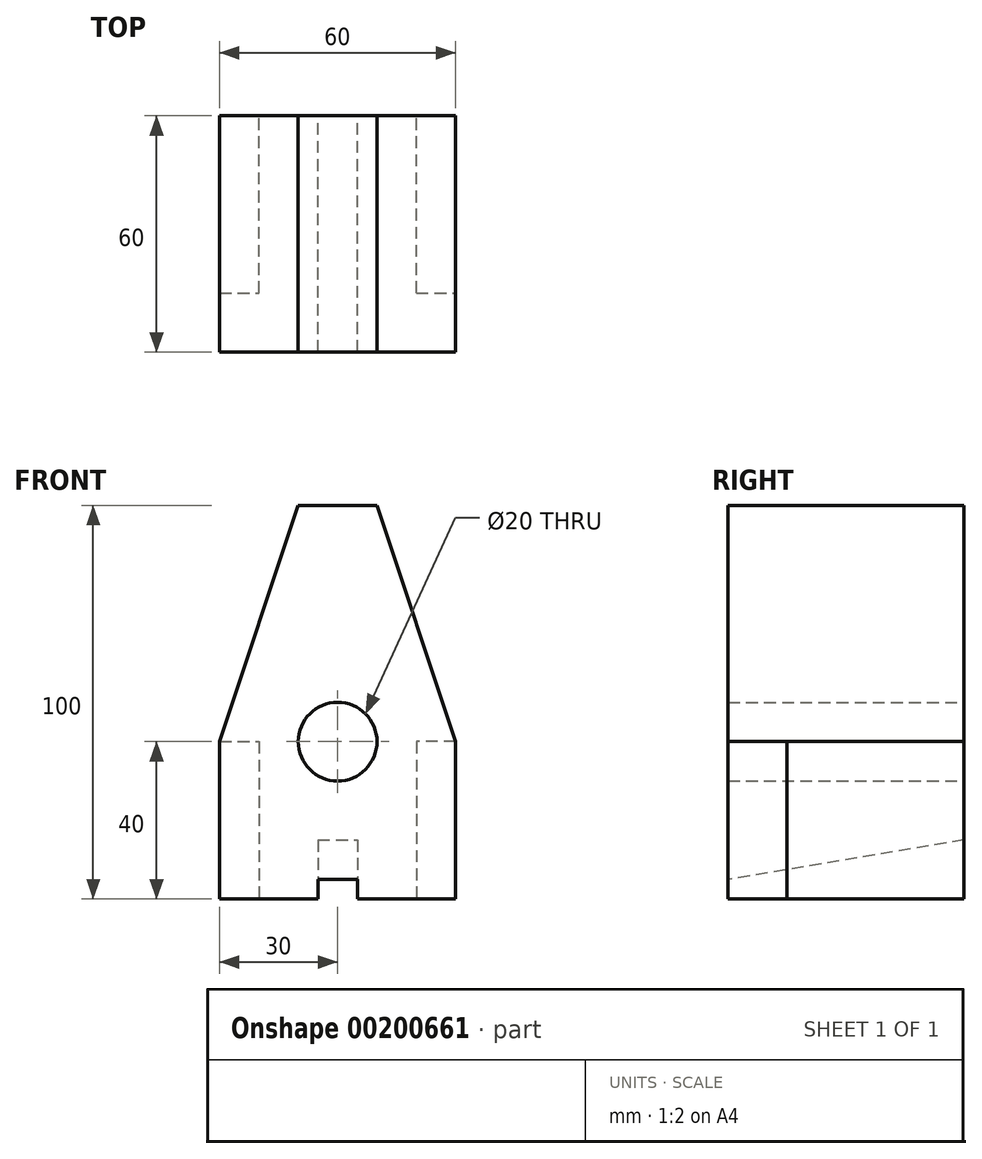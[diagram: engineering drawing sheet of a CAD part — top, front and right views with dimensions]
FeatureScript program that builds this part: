
annotation { "Feature Type Name" : "Feature", "Feature Type Description" : "" }
export const myFeature = defineFeature(function(context is Context, id is Id, definition is map)
    precondition{}
    {
        {
            var Q0;
            Q0=qCreatedBy(makeId("Front.planeOp"),FACE);
            var sketch = newSketch(context, id + "F0", { "sketchPlane" : qUnion([Q0])});
            skLineSegment(sketch, "E0", {"start": v(-30, 0) * mm, "end": v(30, 0) * mm});
            skLineSegment(sketch, "E1", {"start": v(-30, 0) * mm, "end": v(-30, 40) * mm});
            skLineSegment(sketch, "E2", {"start": v(-30, 40) * mm, "end": v(-10, 100) * mm});
            skLineSegment(sketch, "E3", {"start": v(-10, 100) * mm, "end": v(10, 100) * mm});
            skLineSegment(sketch, "E4", {"start": v(30, 0) * mm, "end": v(30, 40) * mm});
            skLineSegment(sketch, "E5", {"start": v(30, 40) * mm, "end": v(10, 100) * mm});
            skCircle(sketch, "E6", {"center": v(0, 40) * mm, "radius": 10 * mm});
            skSolve(sketch);
        }
        {
            var Q0;
            Q0=makeQuery(id+"F0.imprint","IMPRINT",FACE,{"disambiguationData":[TD([[makeQuery(id+"F0.imprint","IMPRINT",EDGE,{"derivedFrom":sQuery(id+"F0.wireOp",EDGE,"E0")}),1.0]])]});
            extrude(context, id + "F1", {"entities" : qUnion([Q0]), "depth" : 60 * mm});
        }
        {
            var Q0;
            Q0=makeQuery(id+"F1.opExtrude","CAP_FACE",FACE,{"disambiguationData":[OSD([sQuery(id+"F0.wireOp",EDGE,"E0"),sQuery(id+"F0.wireOp",EDGE,"E1"),sQuery(id+"F0.wireOp",EDGE,"E2"),sQuery(id+"F0.wireOp",EDGE,"E3"),sQuery(id+"F0.wireOp",EDGE,"E4"),sQuery(id+"F0.wireOp",EDGE,"E5"),sQuery(id+"F0.wireOp",EDGE,"E6")])],"isStart":true});
            var sketch = newSketch(context, id + "F2", { "sketchPlane" : qUnion([Q0])});
            skLineSegment(sketch, "E7.0", {"start": v(30, 0) * mm, "end": v(30, 40) * mm});
            skLineSegment(sketch, "E8.0", {"start": v(-30, 0) * mm, "end": v(-30, 40) * mm});
            skLineSegment(sketch, "E9.0", {"start": v(30, 0) * mm, "end": v(-30, 0) * mm});
            skLineSegment(sketch, "E10", {"start": v(30, 40) * mm, "end": v(20, 40) * mm});
            skLineSegment(sketch, "E11", {"start": v(20, 40) * mm, "end": v(20, 0) * mm});
            skLineSegment(sketch, "E12", {"start": v(-30, 40) * mm, "end": v(-20, 40) * mm});
            skLineSegment(sketch, "E13", {"start": v(-20, 40) * mm, "end": v(-20, 0) * mm});
            skSolve(sketch);
        }
        {
            var Q0;
            Q0 = qSketchRegion(id + "F2", true);
            extrude(context, id + "F3", {"entities" : qUnion([Q0]), "operationType" : NewBodyOperationType.REMOVE, "oppositeDirection" : true, "depth" : 45 * mm});
        }
        {
            var Q0;
            Q0=qCreatedBy(makeId("Right.planeOp"),FACE);
            var sketch = newSketch(context, id + "F4", { "sketchPlane" : qUnion([Q0])});
            skLineSegment(sketch, "E14.0", {"start": v(-60, 0) * mm, "end": v(-60, 5) * mm});
            skLineSegment(sketch, "E15.0", {"start": v(0, 15) * mm, "end": v(0, 0) * mm});
            skLineSegment(sketch, "E16", {"start": v(-60, 0) * mm, "end": v(0, 0) * mm});
            skLineSegment(sketch, "E17.0.0", {"start": v(0, 0) * mm, "end": v(-45, 0) * mm});
            skLineSegment(sketch, "E17.0.2", {"start": v(-45, 0) * mm, "end": v(-60, 0) * mm});
            skLineSegment(sketch, "E17.0.4", {"start": v(-60, 0) * mm, "end": v(-45, 0) * mm});
            skLineSegment(sketch, "E17.0.6", {"start": v(-45, 0) * mm, "end": v(0, 0) * mm});
            skLineSegment(sketch, "E18", {"start": v(0, 15) * mm, "end": v(-60, 5) * mm});
            skPoint(sketch, "E19.orphan", {"position": v(-60, 40) * mm});
            skSolve(sketch);
        }
        {
            var Q0;
            Q0 = qSketchRegion(id + "F4", true);
            extrude(context, id + "F5", {"entities" : qUnion([Q0]), "operationType" : NewBodyOperationType.REMOVE, "endBound" : BoundingType.SYMMETRIC, "oppositeDirection" : true, "depth" : 10 * mm});
        }
    });
